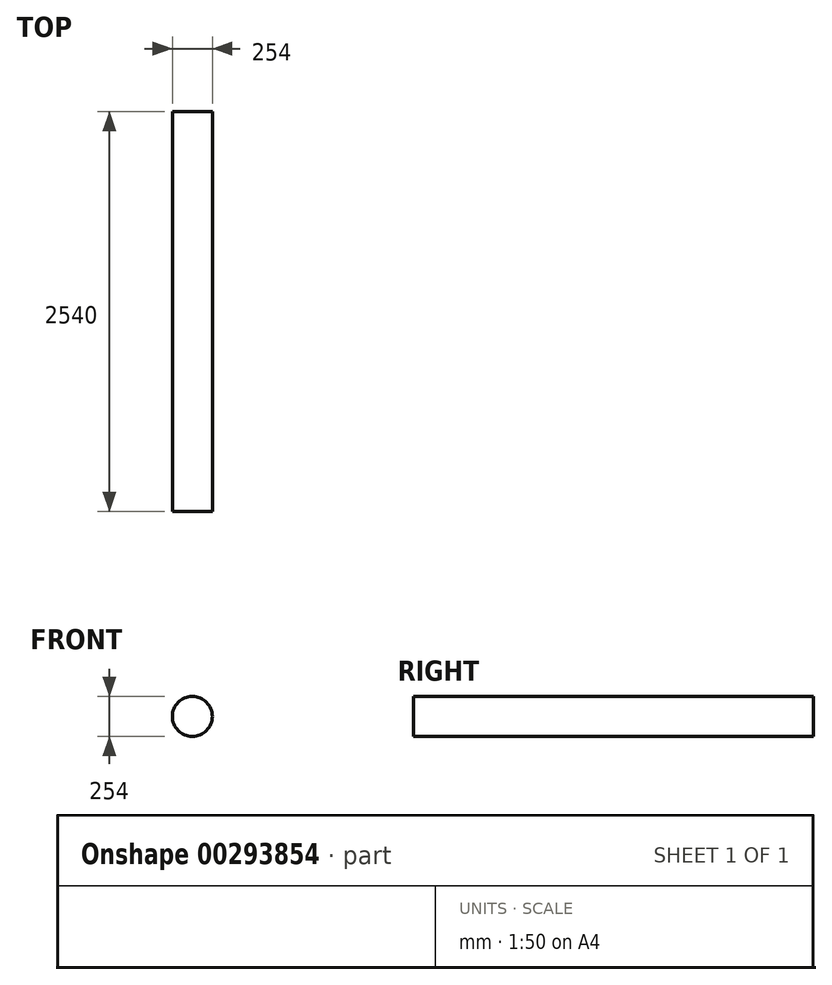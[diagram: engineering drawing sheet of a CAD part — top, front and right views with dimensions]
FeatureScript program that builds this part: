
annotation { "Feature Type Name" : "Feature", "Feature Type Description" : "" }
export const myFeature = defineFeature(function(context is Context, id is Id, definition is map)
    precondition{}
    {
        {
            var Q0;
            Q0=qCreatedBy(makeId("Front.planeOp"),FACE);
            var sketch = newSketch(context, id + "F0", { "sketchPlane" : qUnion([Q0])});
            skCircle(sketch, "E0", {"center": v(0, 0) * mm, "radius": 127 * mm});
            skSolve(sketch);
        }
        {
            var Q0;
            Q0 = qSketchRegion(id + "F0", true);
            extrude(context, id + "F1", {"entities" : qUnion([Q0]), "endBound" : BoundingType.SYMMETRIC, "depth" : 2540 * mm});
        }
    });
